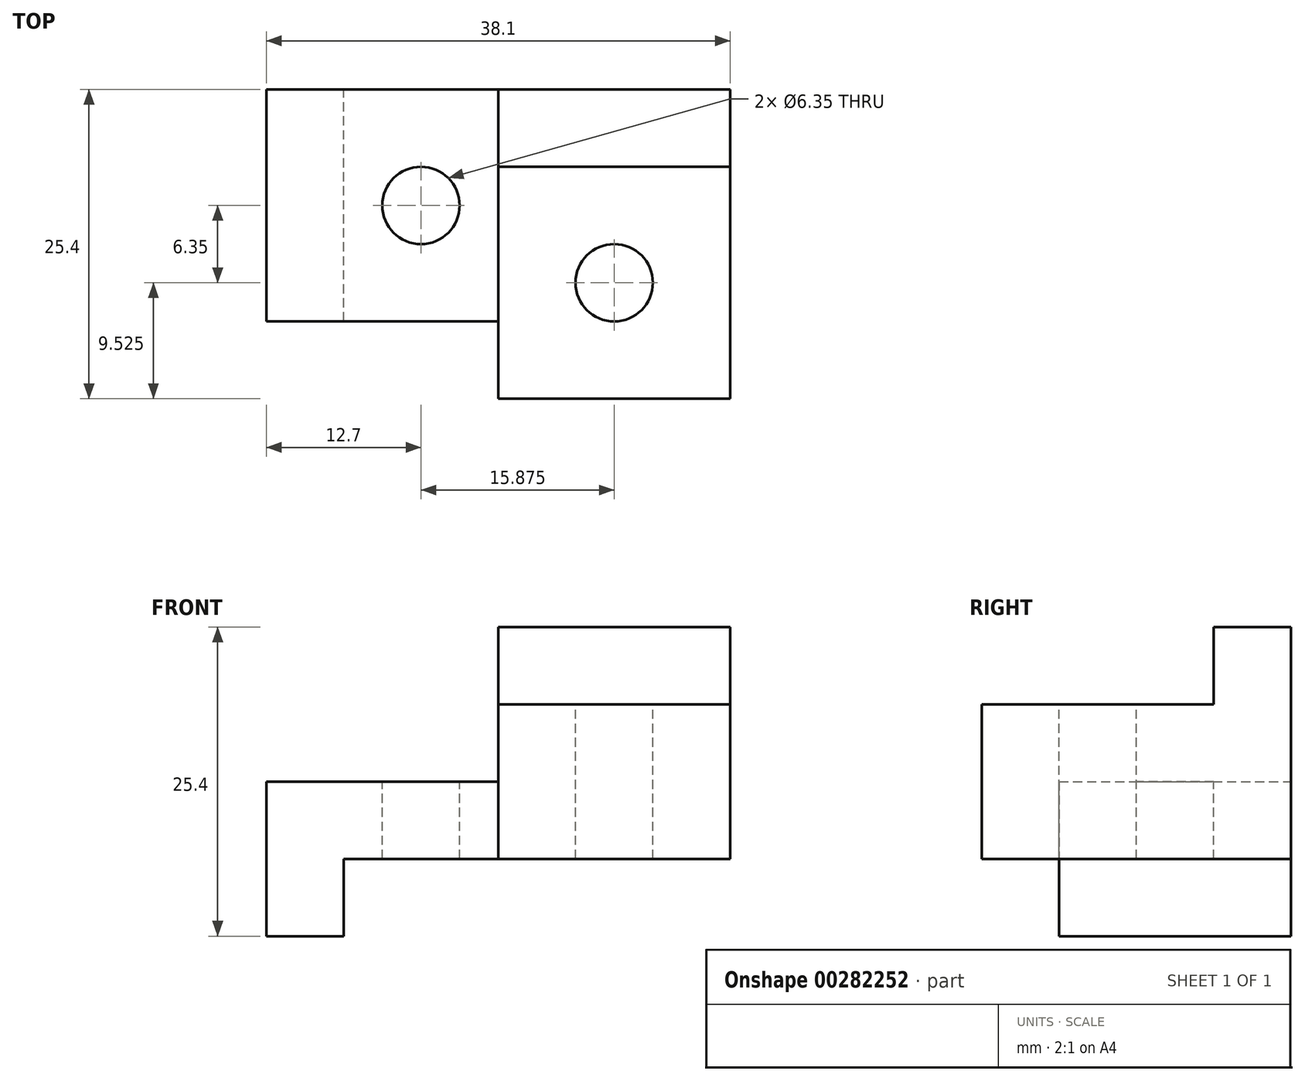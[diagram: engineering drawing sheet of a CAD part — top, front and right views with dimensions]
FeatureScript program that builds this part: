
annotation { "Feature Type Name" : "Feature", "Feature Type Description" : "" }
export const myFeature = defineFeature(function(context is Context, id is Id, definition is map)
    precondition{}
    {
        {
            var Q0;
            Q0=qCreatedBy(makeId("Front.planeOp"),FACE);
            var sketch = newSketch(context, id + "F0", { "sketchPlane" : qUnion([Q0])});
            skLineSegment(sketch, "E0.bottom", {"start": v(0, 0) * mm, "end": v(19.05, 0) * mm});
            skLineSegment(sketch, "E0.top", {"start": v(0, 19.05) * mm, "end": v(19.05, 19.05) * mm});
            skLineSegment(sketch, "E0.left", {"start": v(0, 6.35) * mm, "end": v(0, 19.05) * mm});
            skLineSegment(sketch, "E0.right", {"start": v(19.05, 0) * mm, "end": v(19.05, 19.05) * mm});
            skLineSegment(sketch, "E1", {"start": v(0, 0) * mm, "end": v(-12.7, 0) * mm});
            skLineSegment(sketch, "E2", {"start": v(-12.7, 0) * mm, "end": v(-12.7, -6.35) * mm});
            skLineSegment(sketch, "E3", {"start": v(-12.7, -6.35) * mm, "end": v(-19.05, -6.35) * mm});
            skLineSegment(sketch, "E4", {"start": v(-19.05, -6.35) * mm, "end": v(-19.05, 6.35) * mm});
            skLineSegment(sketch, "E5", {"start": v(-19.05, 6.35) * mm, "end": v(0, 6.35) * mm});
            skLineSegment(sketch, "E6", {"start": v(0, 6.35) * mm, "end": v(0, 0) * mm});
            skSolve(sketch);
        }
        {
            var Q0;
            Q0=makeQuery(id+"F0.imprint","IMPRINT",FACE,{"disambiguationData":[TD([[makeQuery(id+"F0.imprint","IMPRINT",EDGE,{"derivedFrom":sQuery(id+"F0.wireOp",EDGE,"E0.bottom")}),1.0]])]});
            extrude(context, id + "F1", {"entities" : qUnion([Q0]), "depth" : 25.4 * mm});
        }
        {
            var Q0;
            Q0=makeQuery(id+"F0.imprint","IMPRINT",FACE,{"disambiguationData":[TD([[makeQuery(id+"F0.imprint","IMPRINT",EDGE,{"derivedFrom":sQuery(id+"F0.wireOp",EDGE,"E1")}),-1.0]])]});
            extrude(context, id + "F2", {"entities" : qUnion([Q0]), "operationType" : NewBodyOperationType.ADD, "depth" : 19.05 * mm});
        }
        {
            var Q0;
            Q0=makeQuery(id+"F1.opExtrude","CAP_FACE",FACE,{"disambiguationData":[OSD([sQuery(id+"F0.wireOp",EDGE,"E0.bottom"),sQuery(id+"F0.wireOp",EDGE,"E0.top"),sQuery(id+"F0.wireOp",EDGE,"E0.left"),sQuery(id+"F0.wireOp",EDGE,"E0.right"),sQuery(id+"F0.wireOp",EDGE,"E6")])],"isStart":false});
            var sketch = newSketch(context, id + "F3", { "sketchPlane" : qUnion([Q0])});
            skLineSegment(sketch, "E7.bottom", {"start": v(0, 19.05) * mm, "end": v(19.05, 19.05) * mm});
            skLineSegment(sketch, "E7.top", {"start": v(0, 12.7) * mm, "end": v(19.05, 12.7) * mm});
            skLineSegment(sketch, "E7.left", {"start": v(0, 19.05) * mm, "end": v(0, 12.7) * mm});
            skLineSegment(sketch, "E7.right", {"start": v(19.05, 19.05) * mm, "end": v(19.05, 12.7) * mm});
            skSolve(sketch);
        }
        {
            var Q0;
            Q0 = qSketchRegion(id + "F3", true);
            extrude(context, id + "F4", {"entities" : qUnion([Q0]), "operationType" : NewBodyOperationType.REMOVE, "oppositeDirection" : true, "depth" : 19.05 * mm});
        }
        {
            var Q0;
            Q0=makeQuery(id+"F4.boolean.opBoolean","COPY",FACE,{"derivedFrom":makeQuery(id+"F4.opExtrude","SWEPT_FACE",FACE,{"disambiguationData":[OSD([sQuery(id+"F3.wireOp",EDGE,"E7.top")])]})});
            var sketch = newSketch(context, id + "F5", { "sketchPlane" : qUnion([Q0])});
            skCircle(sketch, "E8", {"center": v(9.53, -15.87) * mm, "radius": 3.18 * mm});
            skPoint(sketch, "E8.centerSnap0", {"position": v(0, -15.87) * mm});
            skPoint(sketch, "E8.centerSnap1", {"position": v(9.53, -6.35) * mm});
            skSolve(sketch);
        }
        {
            var Q0;
            Q0=makeQuery(id+"F2.opExtrude","SWEPT_FACE",FACE,{"disambiguationData":[OSD([sQuery(id+"F0.wireOp",EDGE,"E5")])]});
            var sketch = newSketch(context, id + "F6", { "sketchPlane" : qUnion([Q0])});
            skCircle(sketch, "E9", {"center": v(-6.35, -9.53) * mm, "radius": 3.18 * mm});
            skPoint(sketch, "E9.centerSnap0", {"position": v(-19.05, -9.53) * mm});
            skSolve(sketch);
        }
        {
            var Q0;
            Q0=makeQuery(id+"F5.imprint","IMPRINT",FACE,{"disambiguationData":[TD([[makeQuery(id+"F5.imprint","IMPRINT",EDGE,{"derivedFrom":sQuery(id+"F5.wireOp",EDGE,"E8")}),1.0]])]});
            var Q1;
            Q1=makeQuery(id+"F6.imprint","IMPRINT",FACE,{"disambiguationData":[TD([[makeQuery(id+"F6.imprint","IMPRINT",EDGE,{"derivedFrom":sQuery(id+"F6.wireOp",EDGE,"E9")}),1.0]])]});
            extrude(context, id + "F7", {"entities" : qUnion([Q0, Q1]), "operationType" : NewBodyOperationType.REMOVE, "endBound" : BoundingType.THROUGH_ALL, "oppositeDirection" : true, "depth" : 25.4 * mm});
        }
    });
